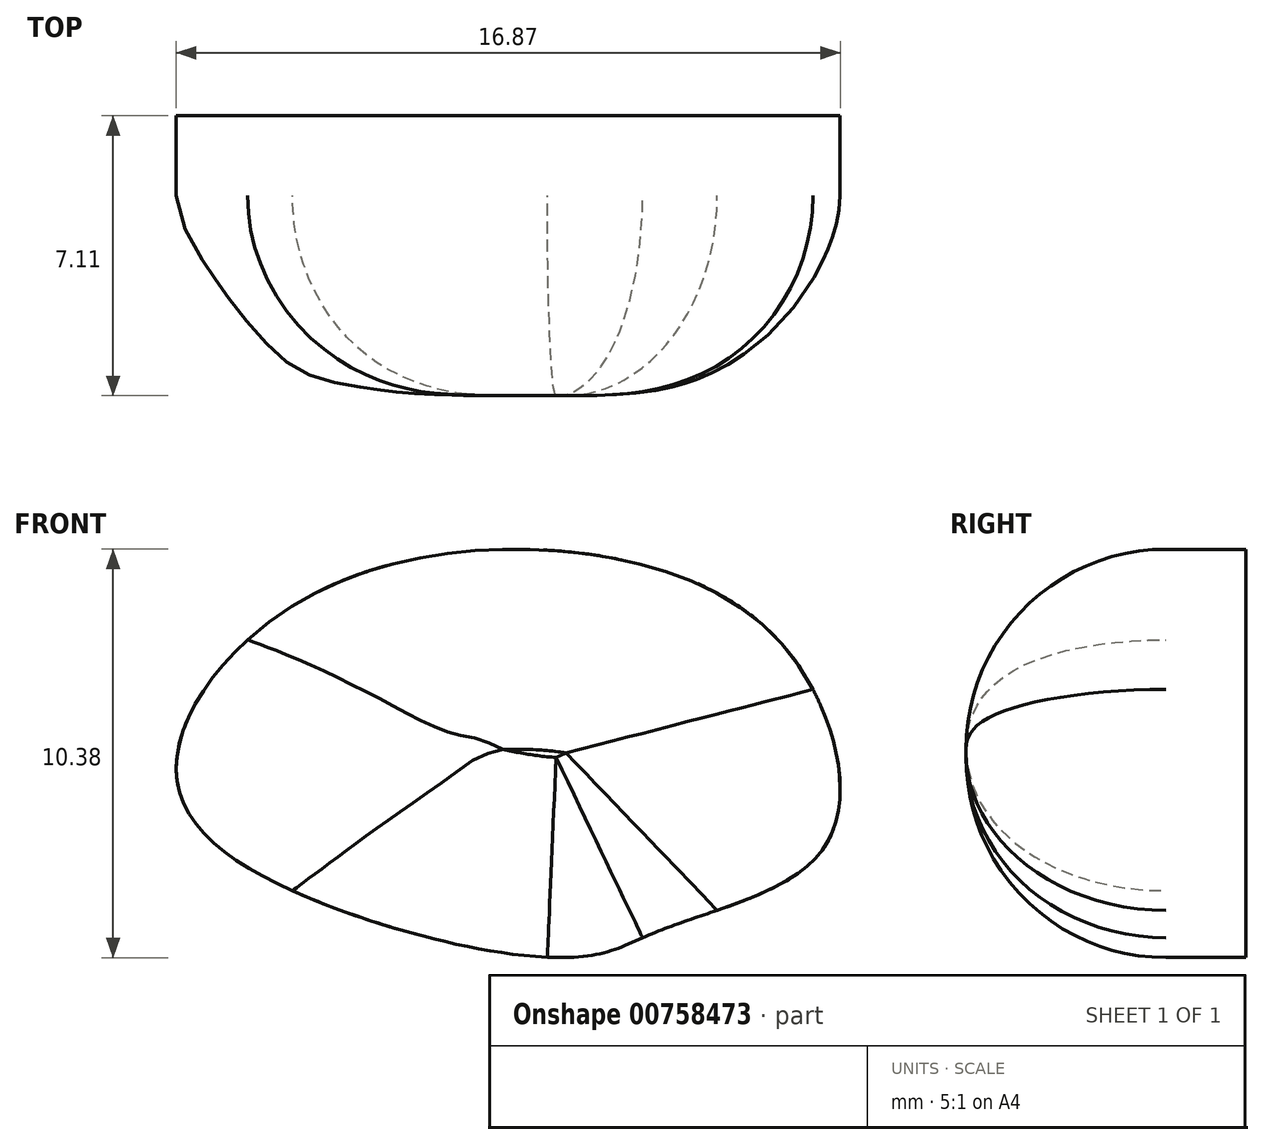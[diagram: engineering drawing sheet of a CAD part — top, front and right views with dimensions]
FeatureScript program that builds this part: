
annotation { "Feature Type Name" : "Feature", "Feature Type Description" : "" }
export const myFeature = defineFeature(function(context is Context, id is Id, definition is map)
    precondition{}
    {
        {
            var Q0;
            Q0=qCreatedBy(makeId("Front.planeOp"),FACE);
            var sketch = newSketch(context, id + "F0", { "sketchPlane" : qUnion([Q0])});
            skFitSpline(sketch, "E0", {"points": [v(0, 0) * mm, v(-3.48, 3.26) * mm, v(-12.67, 2.96) * mm, v(-16.37, -1.78) * mm, v(-12.96, -4.89) * mm, v(-6.15, -6.37) * mm, v(-3.93, -5.63) * mm, v(0, -3.7) * mm, v(0, 0) * mm]});
            skSolve(sketch);
        }
        {
            var Q0;
            Q0 = qSketchRegion(id + "F0", true);
            extrude(context, id + "F1", {"entities" : qUnion([Q0]), "depth" : 7.11 * mm, "offsetDistance" : 25.4 * mm});
        }
        {
            var Q0;
            Q0=makeQuery(id+"F1.opExtrude","CAP_FACE",FACE,{"disambiguationData":[OSD([sQuery(id+"F0.wireOp",EDGE,"E0")])],"isStart":false});
            fillet(context, id + "F2", {"entities" : qUnion([Q0]), "radius" : 5.08 * mm, "tangentPropagation" : true, "allowEdgeOverflow" : false});
        }
    });
